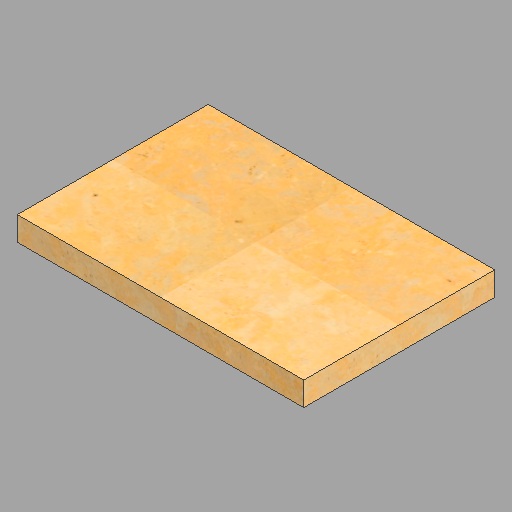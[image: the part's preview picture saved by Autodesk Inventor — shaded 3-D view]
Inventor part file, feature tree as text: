
AUTODESK INVENTOR PART (.ipt)
format: ipt  version: 2023 (Build 270158030, 158C)  size: 248,832 bytes
history: native  units: in
note: dims shown in document units (in); Inventor stores cm internally (conversion verified against a paired STEP export)
features: other x1, extrude x1, sketch x1
ambient origin geometry x8: Origin, YZ Plane, XZ Plane, XY Plane, X Axis, Y Axis, Z Axis, Center Point
bodies: Solid1 (feature_tree)
feature tree (3):
  other  "16x24x2 - 150"
  extrude  "Extrusion1"  Depth=16.0in
  sketch  "Sketch1"  dims[d0=24.0in d1=16.0in d2=2.0in d3=0.0in]
